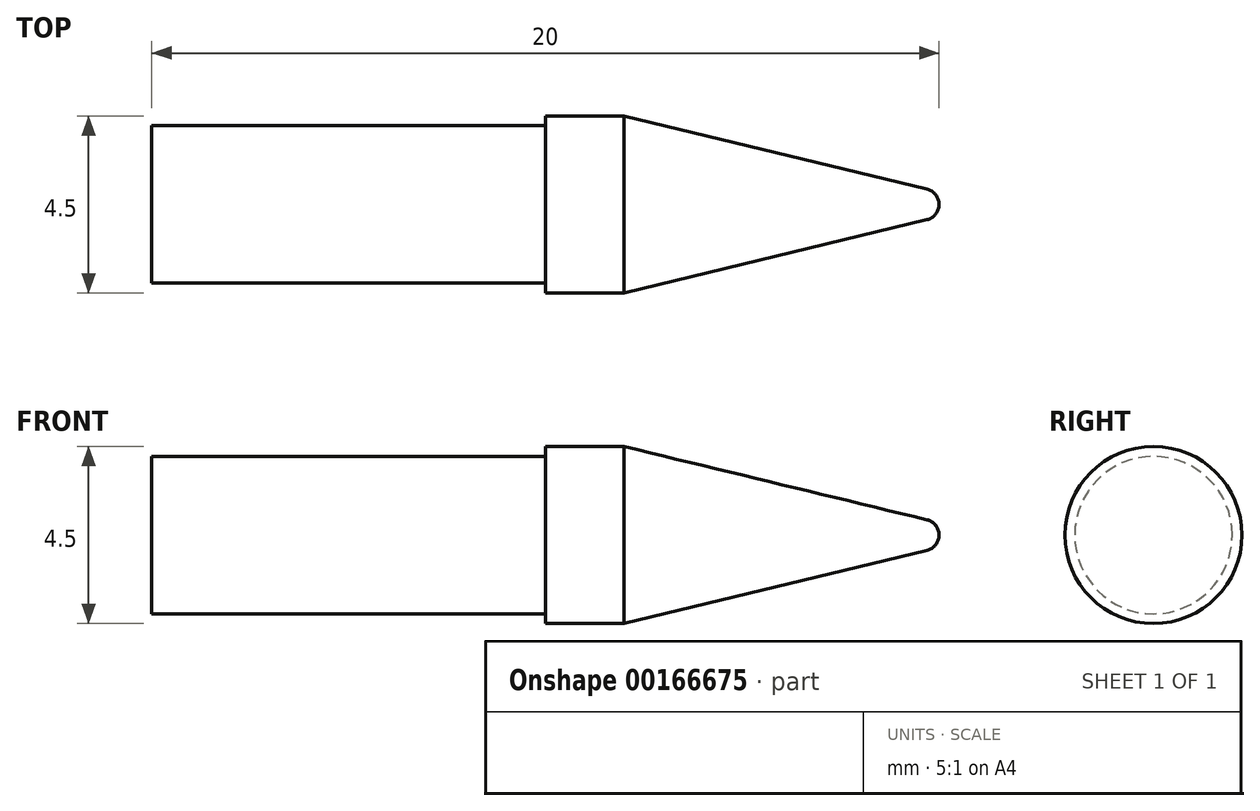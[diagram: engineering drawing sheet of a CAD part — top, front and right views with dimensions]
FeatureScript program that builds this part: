
annotation { "Feature Type Name" : "Feature", "Feature Type Description" : "" }
export const myFeature = defineFeature(function(context is Context, id is Id, definition is map)
    precondition{}
    {
        {
            var Q0;
            Q0=qCreatedBy(makeId("Front.planeOp"),FACE);
            var sketch = newSketch(context, id + "F0", { "sketchPlane" : qUnion([Q0])});
            skLineSegment(sketch, "E0", {"start": v(-4.42, 0) * mm, "end": v(0, 0) * mm, "construction": true});
            skLineSegment(sketch, "E1", {"start": v(0, 2) * mm, "end": v(10, 2) * mm});
            skLineSegment(sketch, "E2", {"start": v(10, 2) * mm, "end": v(10, 2.25) * mm});
            skLineSegment(sketch, "E3", {"start": v(10, 2.25) * mm, "end": v(12, 2.25) * mm});
            skLineSegment(sketch, "E4", {"start": v(12, 2.25) * mm, "end": v(19.7, 0.39) * mm});
            skArc(sketch, "E5", {"start": v(19.7, 0.39) * mm, "mid": v(19.91, 0.25) * mm, "end": v(20, 0) * mm});
            skLineSegment(sketch, "E6", {"start": v(0, 2) * mm, "end": v(0, 0) * mm});
            skLineSegment(sketch, "E7", {"start": v(0, 0) * mm, "end": v(20, 0) * mm});
            skSolve(sketch);
        }
        {
            var Q0;
            Q0=makeQuery(id+"F0.imprint","IMPRINT",FACE,{"disambiguationData":[TD([[makeQuery(id+"F0.imprint","IMPRINT",EDGE,{"derivedFrom":sQuery(id+"F0.wireOp",EDGE,"E1")}),-1.0]])]});
            var Q1;
            Q1=sQuery(id+"F0.wireOp",EDGE,"E0");
            revolve(context, id + "F1", {"entities" : qUnion([Q0]), "axis" : qUnion([Q1]), "revolveType" : RevolveType.FULL});
        }
    });
